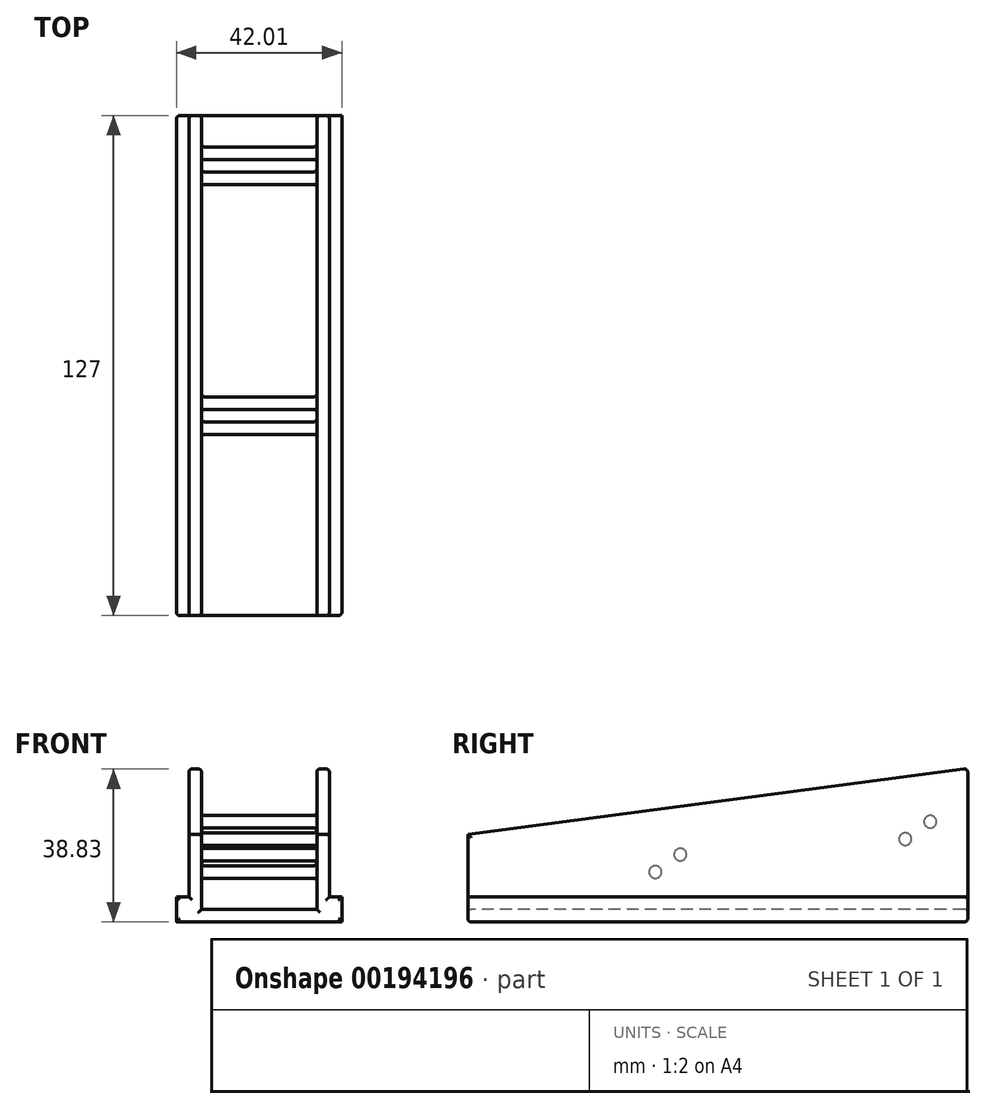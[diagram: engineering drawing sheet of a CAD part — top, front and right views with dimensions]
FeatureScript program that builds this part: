
annotation { "Feature Type Name" : "Feature", "Feature Type Description" : "" }
export const myFeature = defineFeature(function(context is Context, id is Id, definition is map)
    precondition{}
    {
        {
            var Q0;
            Q0=qCreatedBy(makeId("Front.planeOp"),FACE);
            var sketch = newSketch(context, id + "F0", { "sketchPlane" : qUnion([Q0])});
            skLineSegment(sketch, "E0", {"start": v(0, 8.52) * mm, "end": v(0, 0) * mm, "construction": true});
            skLineSegment(sketch, "E1.0", {"start": v(13.51, -0.38) * mm, "end": v(13.51, 50.8) * mm});
            skLineSegment(sketch, "E1.5", {"start": v(-15.8, 50.8) * mm, "end": v(-15.8, -0.38) * mm});
            skLineSegment(sketch, "E1.8", {"start": v(13.51, -0.38) * mm, "end": v(-15.8, -0.38) * mm});
            skLineSegment(sketch, "E2", {"start": v(-15.8, 50.8) * mm, "end": v(-18.97, 50.8) * mm});
            skLineSegment(sketch, "E3", {"start": v(-18.97, 50.8) * mm, "end": v(-18.97, 2.8) * mm});
            skLineSegment(sketch, "E4", {"start": v(-18.97, 2.8) * mm, "end": v(-22.15, 2.8) * mm});
            skLineSegment(sketch, "E5", {"start": v(-22.15, 2.8) * mm, "end": v(-22.15, -3.56) * mm});
            skLineSegment(sketch, "E6", {"start": v(-22.15, -3.56) * mm, "end": v(19.86, -3.56) * mm});
            skCircle(sketch, "E7", {"center": v(0, 5.02) * mm, "radius": 1.7 * mm, "construction": true});
            skLineSegment(sketch, "E8", {"start": v(13.51, 50.8) * mm, "end": v(16.69, 50.8) * mm});
            skLineSegment(sketch, "E9", {"start": v(16.69, 50.8) * mm, "end": v(16.69, 2.8) * mm});
            skLineSegment(sketch, "E10", {"start": v(16.69, 2.8) * mm, "end": v(19.86, 2.8) * mm});
            skLineSegment(sketch, "E11", {"start": v(19.86, 2.8) * mm, "end": v(19.86, -3.56) * mm});
            skSolve(sketch);
        }
        {
            var Q0;
            Q0=makeQuery(id+"F0.imprint","IMPRINT",FACE,{"disambiguationData":[TD([[makeQuery(id+"F0.imprint","IMPRINT",EDGE,{"derivedFrom":sQuery(id+"F0.wireOp",EDGE,"E1.0")}),-1.0]])]});
            extrude(context, id + "F1", {"entities" : qUnion([Q0]), "oppositeDirection" : true, "depth" : 127 * mm});
        }
        {
            var Q0;
            Q0=qCreatedBy(makeId("Right.planeOp"),FACE);
            var sketch = newSketch(context, id + "F2", { "sketchPlane" : qUnion([Q0])});
            skLineSegment(sketch, "E12", {"start": v(0, 4.62) * mm, "end": v(151.1, 24.51) * mm, "construction": true});
            skLineSegment(sketch, "E13.0", {"start": v(0.23, 2.86) * mm, "end": v(151.33, 22.75) * mm, "construction": true});
            skLineSegment(sketch, "E14.0", {"start": v(-0.23, 6.39) * mm, "end": v(150.86, 26.28) * mm, "construction": true});
            skLineSegment(sketch, "E15.0", {"start": v(127, -3.56) * mm, "end": v(0, -3.56) * mm});
            skLineSegment(sketch, "E16.0", {"start": v(0, 50.8) * mm, "end": v(0, 2.8) * mm});
            skLineSegment(sketch, "E17", {"start": v(50.8, -3.56) * mm, "end": v(50.8, 19.59) * mm, "construction": true});
            skLineSegment(sketch, "E18", {"start": v(114.3, -3.56) * mm, "end": v(114.3, 29.1) * mm, "construction": true});
            skLineSegment(sketch, "E19.0", {"start": v(117.47, -3.56) * mm, "end": v(117.47, 29.1) * mm, "construction": true});
            skLineSegment(sketch, "E20.0", {"start": v(111.12, -3.56) * mm, "end": v(111.12, 29.1) * mm, "construction": true});
            skLineSegment(sketch, "E21.0", {"start": v(47.63, -3.56) * mm, "end": v(47.63, 19.59) * mm, "construction": true});
            skLineSegment(sketch, "E22.0", {"start": v(53.98, -3.56) * mm, "end": v(53.98, 19.59) * mm, "construction": true});
            skCircle(sketch, "E23", {"center": v(47.63, 9.1) * mm, "radius": 1.59 * mm});
            skCircle(sketch, "E24", {"center": v(53.98, 13.52) * mm, "radius": 1.59 * mm});
            skCircle(sketch, "E25", {"center": v(111.12, 17.46) * mm, "radius": 1.59 * mm});
            skCircle(sketch, "E26", {"center": v(117.47, 21.88) * mm, "radius": 1.59 * mm});
            skSolve(sketch);
        }
        {
            var Q0;
            Q0 = qSketchRegion(id + "F2", true);
            extrude(context, id + "F3", {"entities" : qUnion([Q0]), "operationType" : NewBodyOperationType.ADD, "endBound" : BoundingType.SYMMETRIC, "depth" : 31.75 * mm});
        }
        {
            var Q0;
            Q0=qCreatedBy(makeId("Right.planeOp"),FACE);
            var sketch = newSketch(context, id + "F4", { "sketchPlane" : qUnion([Q0])});
            skLineSegment(sketch, "E27", {"start": v(0, 18.67) * mm, "end": v(128.45, 35.58) * mm});
            skLineSegment(sketch, "E28", {"start": v(128.45, 35.58) * mm, "end": v(128.45, 57.88) * mm});
            skLineSegment(sketch, "E29", {"start": v(128.45, 57.88) * mm, "end": v(0, 57.88) * mm});
            skLineSegment(sketch, "E30", {"start": v(0, 57.88) * mm, "end": v(0, 18.67) * mm});
            skSolve(sketch);
        }
        {
            var Q0;
            Q0 = qSketchRegion(id + "F4", true);
            extrude(context, id + "F5", {"entities" : qUnion([Q0]), "operationType" : NewBodyOperationType.REMOVE, "endBound" : BoundingType.SYMMETRIC, "oppositeDirection" : true, "depth" : 50.8 * mm});
        }
        {
            var Q0;
            Q0=makeQuery(id+"F5.boolean.opBoolean","INTERSECT",EDGE,{"derivedFrom":[makeQuery(id+"F1.opExtrude","SWEPT_FACE",FACE,{"disambiguationData":[OSD([sQuery(id+"F0.wireOp",EDGE,"E3")])]}),makeQuery(id+"F5.opExtrude","SWEPT_FACE",FACE,{"disambiguationData":[OSD([sQuery(id+"F4.wireOp",EDGE,"E27")])]})]});
            var Q1;
            Q1=makeQuery(id+"F5.boolean.opBoolean","INTERSECT",EDGE,{"derivedFrom":[makeQuery(id+"F1.opExtrude","SWEPT_FACE",FACE,{"disambiguationData":[OSD([sQuery(id+"F0.wireOp",EDGE,"E1.5")])]}),makeQuery(id+"F5.opExtrude","SWEPT_FACE",FACE,{"disambiguationData":[OSD([sQuery(id+"F4.wireOp",EDGE,"E27")])]})]});
            var Q2;
            Q2=makeQuery(id+"F1.opExtrude","CAP_EDGE",EDGE,{"disambiguationData":[OSD([sQuery(id+"F0.wireOp",EDGE,"E1.5")])],"isStart":true});
            var Q3;
            Q3=makeQuery(id+"F1.opExtrude","CAP_EDGE",EDGE,{"disambiguationData":[OSD([sQuery(id+"F0.wireOp",EDGE,"E9")])],"isStart":true});
            var Q4;
            Q4=makeQuery(id+"F5.boolean.opBoolean","INTERSECT",EDGE,{"derivedFrom":[makeQuery(id+"F1.opExtrude","SWEPT_FACE",FACE,{"disambiguationData":[OSD([sQuery(id+"F0.wireOp",EDGE,"E9")])]}),makeQuery(id+"F5.opExtrude","SWEPT_FACE",FACE,{"disambiguationData":[OSD([sQuery(id+"F4.wireOp",EDGE,"E27")])]})]});
            var Q5;
            Q5=makeQuery(id+"F5.boolean.opBoolean","INTERSECT",EDGE,{"derivedFrom":[makeQuery(id+"F1.opExtrude","SWEPT_FACE",FACE,{"disambiguationData":[OSD([sQuery(id+"F0.wireOp",EDGE,"E1.0")])]}),makeQuery(id+"F5.opExtrude","SWEPT_FACE",FACE,{"disambiguationData":[OSD([sQuery(id+"F4.wireOp",EDGE,"E27")])]})]});
            var Q6;
            Q6=makeQuery(id+"F1.opExtrude","CAP_EDGE",EDGE,{"disambiguationData":[OSD([sQuery(id+"F0.wireOp",EDGE,"E1.8")])],"isStart":true});
            var Q7;
            Q7=makeQuery(id+"F1.opExtrude","CAP_EDGE",EDGE,{"disambiguationData":[OSD([sQuery(id+"F0.wireOp",EDGE,"E3")])],"isStart":true});
            var Q8;
            Q8=makeQuery(id+"F1.opExtrude","CAP_EDGE",EDGE,{"disambiguationData":[OSD([sQuery(id+"F0.wireOp",EDGE,"E1.0")])],"isStart":true});
            var Q9;
            Q9=makeQuery(id+"F1.opExtrude","CAP_EDGE",EDGE,{"disambiguationData":[OSD([sQuery(id+"F0.wireOp",EDGE,"E6")])],"isStart":true});
            var Q10;
            Q10=makeQuery(id+"F1.opExtrude","CAP_EDGE",EDGE,{"disambiguationData":[OSD([sQuery(id+"F0.wireOp",EDGE,"E10")])],"isStart":true});
            var Q11;
            Q11=makeQuery(id+"F1.opExtrude","CAP_EDGE",EDGE,{"disambiguationData":[OSD([sQuery(id+"F0.wireOp",EDGE,"E11")])],"isStart":true});
            var Q12;
            Q12=makeQuery(id+"F1.opExtrude","CAP_EDGE",EDGE,{"disambiguationData":[OSD([sQuery(id+"F0.wireOp",EDGE,"E4")])],"isStart":true});
            var Q13;
            Q13=makeQuery(id+"F1.opExtrude","CAP_EDGE",EDGE,{"disambiguationData":[OSD([sQuery(id+"F0.wireOp",EDGE,"E5")])],"isStart":true});
            var Q14;
            Q14=makeQuery(id+"F3.boolean.opBoolean","INTERSECT",EDGE,{"derivedFrom":[makeQuery(id+"F1.opExtrude","SWEPT_FACE",FACE,{"disambiguationData":[OSD([sQuery(id+"F0.wireOp",EDGE,"E1.5")])]}),makeQuery(id+"F3.opExtrude","SWEPT_FACE",FACE,{"disambiguationData":[OSD([sQuery(id+"F2.wireOp",EDGE,"E23")])]})]});
            var Q15;
            Q15=makeQuery(id+"F3.boolean.opBoolean","INTERSECT",EDGE,{"derivedFrom":[makeQuery(id+"F1.opExtrude","SWEPT_FACE",FACE,{"disambiguationData":[OSD([sQuery(id+"F0.wireOp",EDGE,"E1.5")])]}),makeQuery(id+"F3.opExtrude","SWEPT_FACE",FACE,{"disambiguationData":[OSD([sQuery(id+"F2.wireOp",EDGE,"E24")])]})]});
            var Q16;
            Q16=makeQuery(id+"F3.boolean.opBoolean","INTERSECT",EDGE,{"derivedFrom":[makeQuery(id+"F1.opExtrude","SWEPT_FACE",FACE,{"disambiguationData":[OSD([sQuery(id+"F0.wireOp",EDGE,"E1.0")])]}),makeQuery(id+"F3.opExtrude","SWEPT_FACE",FACE,{"disambiguationData":[OSD([sQuery(id+"F2.wireOp",EDGE,"E23")])]})]});
            var Q17;
            Q17=makeQuery(id+"F3.boolean.opBoolean","INTERSECT",EDGE,{"derivedFrom":[makeQuery(id+"F1.opExtrude","SWEPT_FACE",FACE,{"disambiguationData":[OSD([sQuery(id+"F0.wireOp",EDGE,"E1.0")])]}),makeQuery(id+"F3.opExtrude","SWEPT_FACE",FACE,{"disambiguationData":[OSD([sQuery(id+"F2.wireOp",EDGE,"E24")])]})]});
            var Q18;
            Q18=makeQuery(id+"F3.boolean.opBoolean","INTERSECT",EDGE,{"derivedFrom":[makeQuery(id+"F1.opExtrude","SWEPT_FACE",FACE,{"disambiguationData":[OSD([sQuery(id+"F0.wireOp",EDGE,"E1.0")])]}),makeQuery(id+"F3.opExtrude","SWEPT_FACE",FACE,{"disambiguationData":[OSD([sQuery(id+"F2.wireOp",EDGE,"E25")])]})]});
            var Q19;
            Q19=makeQuery(id+"F3.boolean.opBoolean","INTERSECT",EDGE,{"derivedFrom":[makeQuery(id+"F1.opExtrude","SWEPT_FACE",FACE,{"disambiguationData":[OSD([sQuery(id+"F0.wireOp",EDGE,"E1.0")])]}),makeQuery(id+"F3.opExtrude","SWEPT_FACE",FACE,{"disambiguationData":[OSD([sQuery(id+"F2.wireOp",EDGE,"E26")])]})]});
            var Q20;
            Q20=makeQuery(id+"F3.boolean.opBoolean","INTERSECT",EDGE,{"derivedFrom":[makeQuery(id+"F1.opExtrude","SWEPT_FACE",FACE,{"disambiguationData":[OSD([sQuery(id+"F0.wireOp",EDGE,"E1.5")])]}),makeQuery(id+"F3.opExtrude","SWEPT_FACE",FACE,{"disambiguationData":[OSD([sQuery(id+"F2.wireOp",EDGE,"E25")])]})]});
            var Q21;
            Q21=makeQuery(id+"F3.boolean.opBoolean","INTERSECT",EDGE,{"derivedFrom":[makeQuery(id+"F1.opExtrude","SWEPT_FACE",FACE,{"disambiguationData":[OSD([sQuery(id+"F0.wireOp",EDGE,"E1.5")])]}),makeQuery(id+"F3.opExtrude","SWEPT_FACE",FACE,{"disambiguationData":[OSD([sQuery(id+"F2.wireOp",EDGE,"E26")])]})]});
            var Q22;
            Q22=makeQuery(id+"F1.opExtrude","CAP_EDGE",EDGE,{"disambiguationData":[OSD([sQuery(id+"F0.wireOp",EDGE,"E9")])],"isStart":false});
            var Q23;
            Q23=makeQuery(id+"F1.opExtrude","CAP_EDGE",EDGE,{"disambiguationData":[OSD([sQuery(id+"F0.wireOp",EDGE,"E10")])],"isStart":false});
            var Q24;
            Q24=makeQuery(id+"F1.opExtrude","CAP_EDGE",EDGE,{"disambiguationData":[OSD([sQuery(id+"F0.wireOp",EDGE,"E6")])],"isStart":false});
            var Q25;
            Q25=makeQuery(id+"F1.opExtrude","CAP_EDGE",EDGE,{"disambiguationData":[OSD([sQuery(id+"F0.wireOp",EDGE,"E5")])],"isStart":false});
            var Q26;
            Q26=makeQuery(id+"F1.opExtrude","CAP_EDGE",EDGE,{"disambiguationData":[OSD([sQuery(id+"F0.wireOp",EDGE,"E4")])],"isStart":false});
            var Q27;
            Q27=makeQuery(id+"F1.opExtrude","CAP_EDGE",EDGE,{"disambiguationData":[OSD([sQuery(id+"F0.wireOp",EDGE,"E3")])],"isStart":false});
            var Q28;
            Q28=makeQuery(id+"F1.opExtrude","CAP_EDGE",EDGE,{"disambiguationData":[OSD([sQuery(id+"F0.wireOp",EDGE,"E1.5")])],"isStart":false});
            var Q29;
            Q29=makeQuery(id+"F5.boolean.opBoolean","INTERSECT",EDGE,{"disambiguationData":[OD(1.0)],"derivedFrom":[makeQuery(id+"F1.opExtrude","CAP_FACE",FACE,{"disambiguationData":[OSD([sQuery(id+"F0.wireOp",EDGE,"E1.0"),sQuery(id+"F0.wireOp",EDGE,"E1.5"),sQuery(id+"F0.wireOp",EDGE,"E1.8"),sQuery(id+"F0.wireOp",EDGE,"E2"),sQuery(id+"F0.wireOp",EDGE,"E3"),sQuery(id+"F0.wireOp",EDGE,"E4"),sQuery(id+"F0.wireOp",EDGE,"E5"),sQuery(id+"F0.wireOp",EDGE,"E6"),sQuery(id+"F0.wireOp",EDGE,"E8"),sQuery(id+"F0.wireOp",EDGE,"E9"),sQuery(id+"F0.wireOp",EDGE,"E10"),sQuery(id+"F0.wireOp",EDGE,"E11")])],"isStart":false}),makeQuery(id+"F5.opExtrude","SWEPT_FACE",FACE,{"disambiguationData":[OSD([sQuery(id+"F4.wireOp",EDGE,"E27")])]})]});
            var Q30;
            Q30=makeQuery(id+"F1.opExtrude","CAP_EDGE",EDGE,{"disambiguationData":[OSD([sQuery(id+"F0.wireOp",EDGE,"E1.8")])],"isStart":false});
            var Q31;
            {var subQ0=sQuery(id+"F0.wireOp",EDGE,"E1.0");var subQ2=sQuery(id+"F4.wireOp",EDGE,"E27");Q31=makeQuery(id+"F5.boolean.opBoolean","COPY",EDGE,{"disambiguationData":[TD([makeQuery(id+"F1.opExtrude","SWEPT_FACE",FACE,{"disambiguationData":[OSD([subQ0])]})])],"derivedFrom":makeQuery(id+"F5.opExtrude","SWEPT_EDGE",EDGE,{"disambiguationData":[OSD([subQ2,sQuery(id+"F4.wireOp",EDGE,"E30")])]})});}
            var Q32;
            {var subQ1=sQuery(id+"F0.wireOp",EDGE,"E1.5");var subQ2=sQuery(id+"F4.wireOp",EDGE,"E27");Q32=makeQuery(id+"F5.boolean.opBoolean","COPY",EDGE,{"disambiguationData":[TD([makeQuery(id+"F1.opExtrude","SWEPT_FACE",FACE,{"disambiguationData":[OSD([subQ1])]})])],"derivedFrom":makeQuery(id+"F5.opExtrude","SWEPT_EDGE",EDGE,{"disambiguationData":[OSD([subQ2,sQuery(id+"F4.wireOp",EDGE,"E30")])]})});}
            var Q33;
            Q33=makeQuery(id+"F5.boolean.opBoolean","INTERSECT",EDGE,{"disambiguationData":[OD(0.0)],"derivedFrom":[makeQuery(id+"F1.opExtrude","CAP_FACE",FACE,{"disambiguationData":[OSD([sQuery(id+"F0.wireOp",EDGE,"E1.0"),sQuery(id+"F0.wireOp",EDGE,"E1.5"),sQuery(id+"F0.wireOp",EDGE,"E1.8"),sQuery(id+"F0.wireOp",EDGE,"E2"),sQuery(id+"F0.wireOp",EDGE,"E3"),sQuery(id+"F0.wireOp",EDGE,"E4"),sQuery(id+"F0.wireOp",EDGE,"E5"),sQuery(id+"F0.wireOp",EDGE,"E6"),sQuery(id+"F0.wireOp",EDGE,"E8"),sQuery(id+"F0.wireOp",EDGE,"E9"),sQuery(id+"F0.wireOp",EDGE,"E10"),sQuery(id+"F0.wireOp",EDGE,"E11")])],"isStart":false}),makeQuery(id+"F5.opExtrude","SWEPT_FACE",FACE,{"disambiguationData":[OSD([sQuery(id+"F4.wireOp",EDGE,"E27")])]})]});
            var Q34;
            Q34=makeQuery(id+"F1.opExtrude","CAP_EDGE",EDGE,{"disambiguationData":[OSD([sQuery(id+"F0.wireOp",EDGE,"E1.0")])],"isStart":false});
            fillet(context, id + "F6", {"entities" : qUnion([Q0, Q1, Q2, Q3, Q4, Q5, Q6, Q7, Q8, Q9, Q10, Q11, Q12, Q13, Q14, Q15, Q16, Q17, Q18, Q19, Q20, Q21, Q22, Q23, Q24, Q25, Q26, Q27, Q28, Q29, Q30, Q31, Q32, Q33, Q34]), "radius" : 0.81 * mm, "tangentPropagation" : true, "allowEdgeOverflow" : false});
        }
    });
